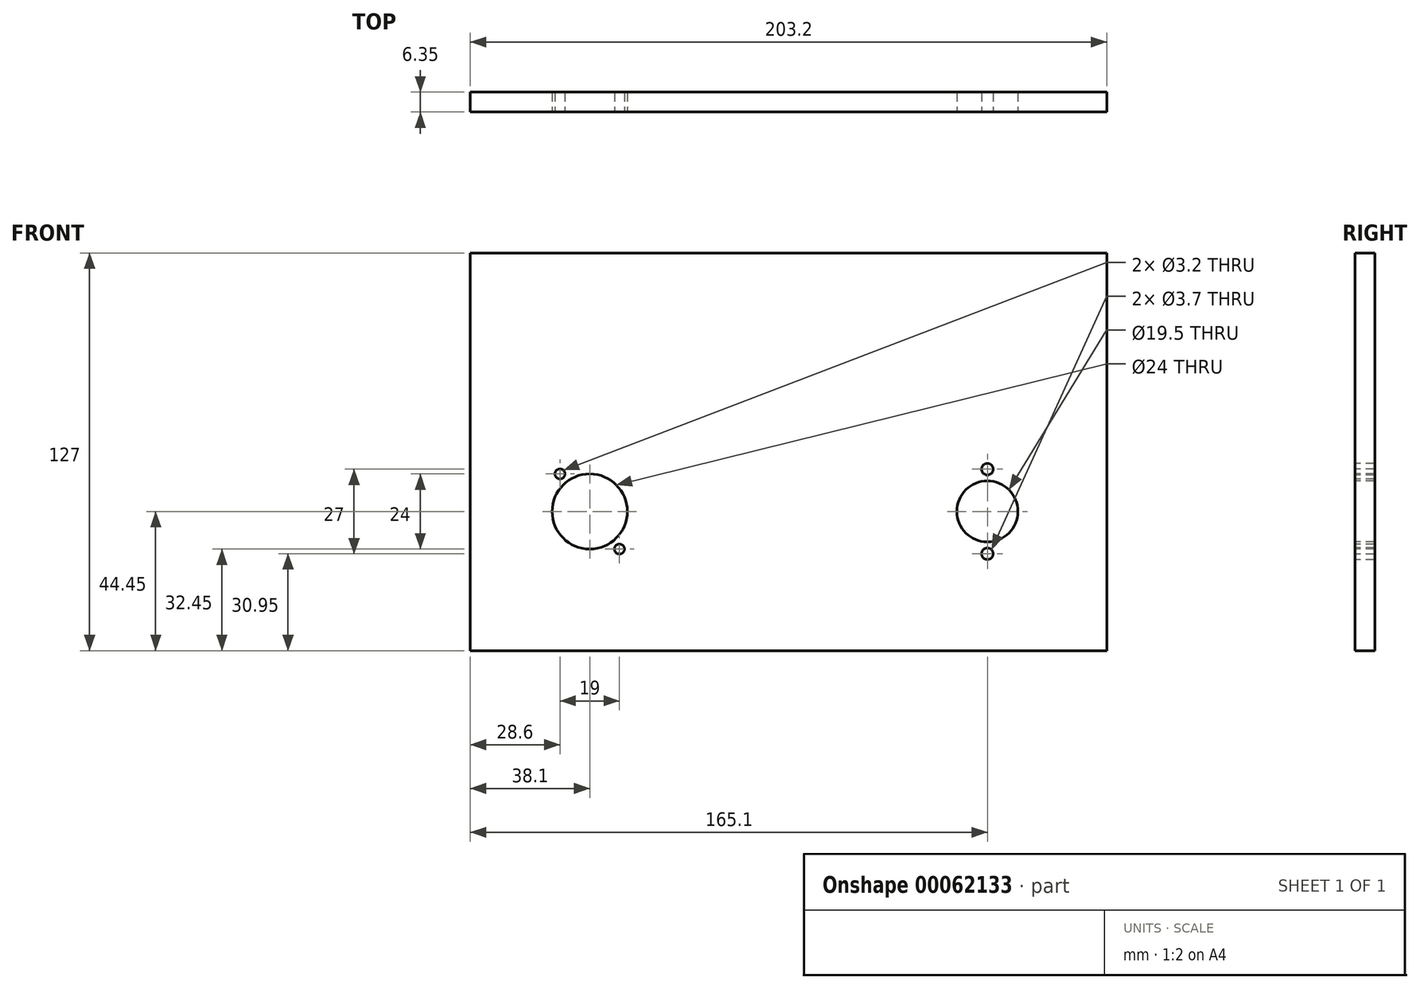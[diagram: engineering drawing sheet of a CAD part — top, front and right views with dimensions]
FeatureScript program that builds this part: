
annotation { "Feature Type Name" : "Feature", "Feature Type Description" : "" }
export const myFeature = defineFeature(function(context is Context, id is Id, definition is map)
    precondition{}
    {
        {
            var Q0;
            Q0=qCreatedBy(makeId("Front.planeOp"),FACE);
            var sketch = newSketch(context, id + "F0", { "sketchPlane" : qUnion([Q0])});
            skLineSegment(sketch, "E0.rect.bottom", {"start": v(101.6, 63.5) * mm, "end": v(-101.6, 63.5) * mm});
            skLineSegment(sketch, "E0.rect.top", {"start": v(101.6, -63.5) * mm, "end": v(-101.6, -63.5) * mm});
            skLineSegment(sketch, "E0.rect.left", {"start": v(101.6, 63.5) * mm, "end": v(101.6, -63.5) * mm});
            skLineSegment(sketch, "E0.rect.right", {"start": v(-101.6, 63.5) * mm, "end": v(-101.6, -63.5) * mm});
            skPoint(sketch, "E0.rect.middle", {"position": v(0, 0) * mm});
            skSolve(sketch);
        }
        {
            var Q0;
            Q0 = qSketchRegion(id + "F0", true);
            extrude(context, id + "F1", {"entities" : qUnion([Q0]), "depth" : 6.35 * mm, "offsetDistance" : 25.4 * mm});
        }
        {
            var Q0;
            Q0=makeQuery(id+"F1.opExtrude","CAP_FACE",FACE,{"disambiguationData":[OSD([sQuery(id+"F0.wireOp",EDGE,"E0.rect.bottom"),sQuery(id+"F0.wireOp",EDGE,"E0.rect.top"),sQuery(id+"F0.wireOp",EDGE,"E0.rect.left"),sQuery(id+"F0.wireOp",EDGE,"E0.rect.right")])],"isStart":false});
            var sketch = newSketch(context, id + "F2", { "sketchPlane" : qUnion([Q0])});
            skLineSegment(sketch, "E1", {"start": v(-63.5, 63.5) * mm, "end": v(-63.5, -63.5) * mm});
            skCircle(sketch, "E2", {"center": v(-63.5, -19.05) * mm, "radius": 12 * mm});
            skCircle(sketch, "E3", {"center": v(-73, -7.05) * mm, "radius": 1.6 * mm});
            skCircle(sketch, "E4", {"center": v(-54, -31.05) * mm, "radius": 1.6 * mm});
            skLineSegment(sketch, "E5", {"start": v(63.5, 63.5) * mm, "end": v(63.5, -63.5) * mm});
            skCircle(sketch, "E6", {"center": v(63.5, -19.05) * mm, "radius": 9.75 * mm});
            skCircle(sketch, "E7", {"center": v(63.5, -5.55) * mm, "radius": 1.85 * mm});
            skCircle(sketch, "E8", {"center": v(63.5, -32.55) * mm, "radius": 1.85 * mm});
            skSolve(sketch);
        }
        {
            var Q0;
            Q0 = qSketchRegion(id + "F2", true);
            extrude(context, id + "F3", {"entities" : qUnion([Q0]), "operationType" : NewBodyOperationType.REMOVE, "endBound" : BoundingType.UP_TO_NEXT, "oppositeDirection" : true, "depth" : 25.4 * mm, "offsetDistance" : 25.4 * mm});
        }
    });
